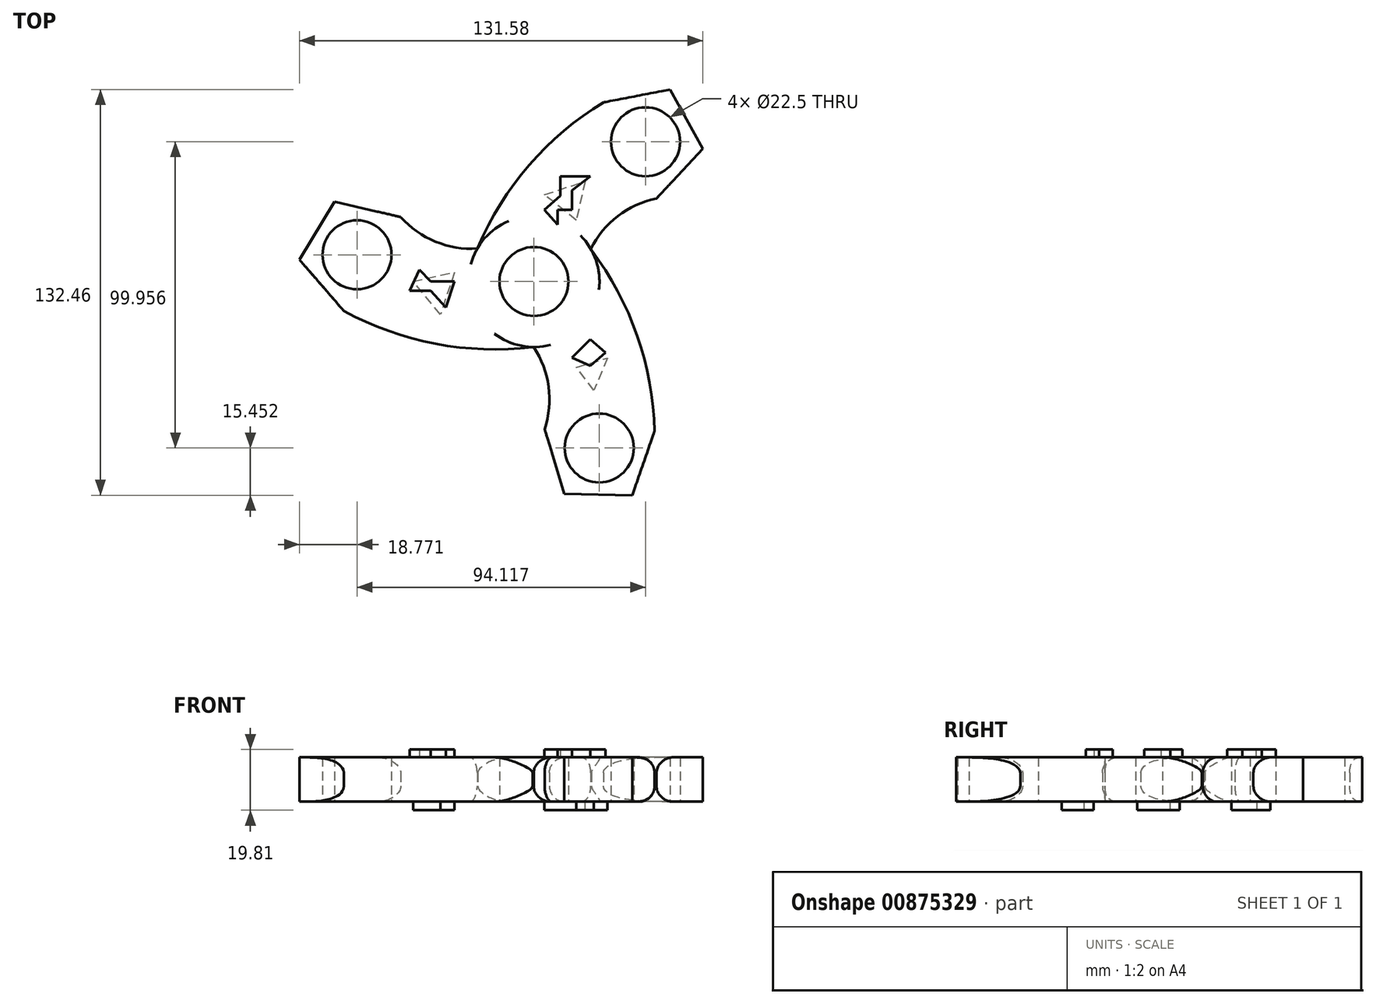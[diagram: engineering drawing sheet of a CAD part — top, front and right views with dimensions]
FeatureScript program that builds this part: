
annotation { "Feature Type Name" : "Feature", "Feature Type Description" : "" }
export const myFeature = defineFeature(function(context is Context, id is Id, definition is map)
    precondition{}
    {
        {
            var Q0;
            Q0=qCreatedBy(makeId("Top.planeOp"),FACE);
            var sketch = newSketch(context, id + "F0", { "sketchPlane" : qUnion([Q0])});
            skCircle(sketch, "E0", {"center": v(0, 0) * mm, "radius": 11.25 * mm});
            skCircle(sketch, "E1", {"center": v(0, 0) * mm, "radius": 21.38 * mm});
            skCircle(sketch, "E2", {"center": v(36.4, 45.62) * mm, "radius": 11.25 * mm});
            skCircle(sketch, "E3.cCircle", {"center": v(36.4, 45.62) * mm, "radius": 15.24 * mm, "construction": true});
            skLineSegment(sketch, "E3.0", {"start": v(22.66, 58.5) * mm, "end": v(44.4, 62.67) * mm});
            skLineSegment(sketch, "E3.1", {"start": v(44.4, 62.67) * mm, "end": v(55.1, 43.28) * mm});
            skLineSegment(sketch, "E3.2", {"start": v(55.1, 43.28) * mm, "end": v(39.96, 27.12) * mm});
            skLineSegment(sketch, "E3.3", {"start": v(39.96, 27.12) * mm, "end": v(19.91, 36.52) * mm});
            skLineSegment(sketch, "E3.4", {"start": v(19.91, 36.52) * mm, "end": v(22.66, 58.5) * mm});
            skPoint(sketch, "E3.0.midPoint", {"position": v(33.53, 60.58) * mm});
            skArc(sketch, "E4", {"start": v(22.66, 58.5) * mm, "mid": v(-1.53, 38) * mm, "end": v(-18.29, 11.09) * mm});
            skArc(sketch, "E5", {"start": v(39.96, 27.12) * mm, "mid": v(27.36, 21.33) * mm, "end": v(18.57, 10.61) * mm});
            skCircle(sketch, "E6.1.0", {"center": v(-57.7, 8.72) * mm, "radius": 15.24 * mm, "construction": true});
            skArc(sketch, "E6.1.1", {"start": v(-61.98, -9.63) * mm, "mid": v(-32.14, -20.32) * mm, "end": v(-0.46, -21.38) * mm});
            skCircle(sketch, "E6.1.2", {"center": v(-57.7, 8.72) * mm, "radius": 11.25 * mm});
            skLineSegment(sketch, "E6.1.3", {"start": v(-41.58, -1.01) * mm, "end": v(-61.98, -9.63) * mm});
            skPoint(sketch, "E6.1.4", {"position": v(-69.23, -1.25) * mm});
            skLineSegment(sketch, "E6.1.6", {"start": v(-43.47, 21.05) * mm, "end": v(-41.58, -1.01) * mm});
            skArc(sketch, "E6.1.7", {"start": v(-43.47, 21.05) * mm, "mid": v(-32.15, 13.03) * mm, "end": v(-18.47, 10.77) * mm});
            skLineSegment(sketch, "E6.1.9", {"start": v(-65.04, 26.08) * mm, "end": v(-43.47, 21.05) * mm});
            skLineSegment(sketch, "E6.1.10", {"start": v(-61.98, -9.63) * mm, "end": v(-76.48, 7.12) * mm});
            skLineSegment(sketch, "E6.1.11", {"start": v(-76.48, 7.12) * mm, "end": v(-65.04, 26.08) * mm});
            skCircle(sketch, "E6.2.0", {"center": v(21.3, -54.34) * mm, "radius": 15.24 * mm, "construction": true});
            skArc(sketch, "E6.2.1", {"start": v(39.33, -48.87) * mm, "mid": v(33.67, -17.68) * mm, "end": v(18.74, 10.3) * mm});
            skCircle(sketch, "E6.2.2", {"center": v(21.3, -54.34) * mm, "radius": 11.25 * mm});
            skLineSegment(sketch, "E6.2.3", {"start": v(21.67, -35.5) * mm, "end": v(39.33, -48.87) * mm});
            skPoint(sketch, "E6.2.4", {"position": v(35.7, -59.33) * mm});
            skLineSegment(sketch, "E6.2.6", {"start": v(3.5, -48.17) * mm, "end": v(21.67, -35.5) * mm});
            skArc(sketch, "E6.2.7", {"start": v(3.5, -48.17) * mm, "mid": v(4.79, -34.36) * mm, "end": v(-0.1, -21.38) * mm});
            skLineSegment(sketch, "E6.2.9", {"start": v(9.94, -69.36) * mm, "end": v(3.5, -48.17) * mm});
            skLineSegment(sketch, "E6.2.10", {"start": v(39.33, -48.87) * mm, "end": v(32.08, -69.8) * mm});
            skLineSegment(sketch, "E6.2.11", {"start": v(32.08, -69.8) * mm, "end": v(9.94, -69.36) * mm});
            skSolve(sketch);
        }
        {
            var Q0;
            Q0=makeQuery(id+"F0.imprint","IMPRINT",FACE,{"disambiguationData":[TD([[makeQuery(id+"F0.imprint","IMPRINT",EDGE,{"derivedFrom":sQuery(id+"F0.wireOp",EDGE,"E0")}),-1.0]])]});
            var Q1;
            Q1=makeQuery(id+"F0.imprint","IMPRINT",FACE,{"disambiguationData":[TD([[makeQuery(id+"F0.imprint","IMPRINT",EDGE,{"derivedFrom":sQuery(id+"F0.wireOp",EDGE,"E3.3")}),1.0]])]});
            var Q2;
            {var subQ1=sQuery(id+"F0.wireOp",EDGE,"E6.2.1");Q2=makeQuery(id+"F0.imprint","IMPRINT",FACE,{"disambiguationData":[TD([[makeQuery(id+"F0.imprint","IMPRINT",EDGE,{"derivedFrom":subQ1}),1.0]])]});}
            var Q3;
            {var subQ1=sQuery(id+"F0.wireOp",EDGE,"E6.1.1");Q3=makeQuery(id+"F0.imprint","IMPRINT",FACE,{"disambiguationData":[TD([[makeQuery(id+"F0.imprint","IMPRINT",EDGE,{"derivedFrom":subQ1}),1.0]])]});}
            var Q4;
            Q4=makeQuery(id+"F0.imprint","IMPRINT",FACE,{"disambiguationData":[TD([[makeQuery(id+"F0.imprint","IMPRINT",EDGE,{"derivedFrom":sQuery(id+"F0.wireOp",EDGE,"E6.1.2")}),-1.0]])]});
            var Q5;
            Q5=makeQuery(id+"F0.imprint","IMPRINT",FACE,{"disambiguationData":[TD([[makeQuery(id+"F0.imprint","IMPRINT",EDGE,{"derivedFrom":sQuery(id+"F0.wireOp",EDGE,"E2")}),-1.0]])]});
            var Q6;
            Q6=makeQuery(id+"F0.imprint","IMPRINT",FACE,{"disambiguationData":[TD([[makeQuery(id+"F0.imprint","IMPRINT",EDGE,{"derivedFrom":sQuery(id+"F0.wireOp",EDGE,"E6.2.2")}),-1.0]])]});
            extrude(context, id + "F1", {"entities" : qUnion([Q0, Q1, Q2, Q3, Q4, Q5, Q6]), "depth" : 14.48 * mm, "offsetDistance" : 25.4 * mm});
        }
        {
            var Q0;
            Q0=qCreatedBy(makeId("Top.planeOp"),FACE);
            var sketch = newSketch(context, id + "F2", { "sketchPlane" : qUnion([Q0])});
            skLineSegment(sketch, "E7", {"start": v(-30.5, -10.8) * mm, "end": v(-39.42, 0) * mm});
            skLineSegment(sketch, "E8", {"start": v(-39.42, 0) * mm, "end": v(-25.9, 3.02) * mm});
            skLineSegment(sketch, "E9", {"start": v(-25.9, 3.02) * mm, "end": v(-30.5, -10.8) * mm});
            skLineSegment(sketch, "E10", {"start": v(13.82, 20) * mm, "end": v(3.46, 28.35) * mm});
            skLineSegment(sketch, "E11", {"start": v(3.46, 28.35) * mm, "end": v(16.7, 32.67) * mm});
            skLineSegment(sketch, "E12", {"start": v(16.7, 32.67) * mm, "end": v(13.82, 20) * mm});
            skLineSegment(sketch, "E13", {"start": v(19.55, -35.48) * mm, "end": v(13.82, -28.06) * mm});
            skLineSegment(sketch, "E14", {"start": v(13.82, -28.06) * mm, "end": v(23.94, -25.02) * mm});
            skLineSegment(sketch, "E15", {"start": v(23.94, -25.02) * mm, "end": v(19.55, -35.48) * mm});
            skSolve(sketch);
        }
        {
            var Q0;
            Q0 = qSketchRegion(id + "F2", true);
            extrude(context, id + "F3", {"entities" : qUnion([Q0]), "operationType" : NewBodyOperationType.ADD, "oppositeDirection" : true, "depth" : 2.8 * mm, "offsetDistance" : 25.4 * mm});
        }
        {
            var Q0;
            Q0=makeQuery(id+"F1.opExtrude","CAP_FACE",FACE,{"disambiguationData":[OSD([sQuery(id+"F0.wireOp",EDGE,"E2"),sQuery(id+"F0.wireOp",EDGE,"E3.0"),sQuery(id+"F0.wireOp",EDGE,"E3.1"),sQuery(id+"F0.wireOp",EDGE,"E3.2"),sQuery(id+"F0.wireOp",EDGE,"E4"),sQuery(id+"F0.wireOp",EDGE,"E5"),sQuery(id+"F0.wireOp",EDGE,"E6.1.1"),sQuery(id+"F0.wireOp",EDGE,"E6.1.2"),sQuery(id+"F0.wireOp",EDGE,"E6.1.7"),sQuery(id+"F0.wireOp",EDGE,"E6.1.9"),sQuery(id+"F0.wireOp",EDGE,"E6.1.10"),sQuery(id+"F0.wireOp",EDGE,"E6.1.11"),sQuery(id+"F0.wireOp",EDGE,"E6.2.1"),sQuery(id+"F0.wireOp",EDGE,"E6.2.2"),sQuery(id+"F0.wireOp",EDGE,"E1"),sQuery(id+"F0.wireOp",EDGE,"E6.2.7"),sQuery(id+"F0.wireOp",EDGE,"E0"),sQuery(id+"F0.wireOp",EDGE,"E6.2.9"),sQuery(id+"F0.wireOp",EDGE,"E6.2.10"),sQuery(id+"F0.wireOp",EDGE,"E6.2.11")])],"isStart":false});
            var sketch = newSketch(context, id + "F4", { "sketchPlane" : qUnion([Q0])});
            skSolve(sketch);
        }
        {
            var Q0;
            Q0=makeQuery(id+"F4.imprint","IMPRINT",FACE,{"disambiguationData":[TD([[makeQuery(id+"F4.imprint","IMPRINT",EDGE,{"derivedFrom":makeQuery(id+"F1.opExtrude","CAP_EDGE",EDGE,{"disambiguationData":[OSD([sQuery(id+"F0.wireOp",EDGE,"E2")])],"isStart":false})}),-1.0]])]});
            var sketch = newSketch(context, id + "F5", { "sketchPlane" : qUnion([Q0])});
            skLineSegment(sketch, "E16", {"start": v(-37.41, 3.89) * mm, "end": v(-40.58, -3.02) * mm});
            skLineSegment(sketch, "E17", {"start": v(-40.58, -3.02) * mm, "end": v(-33.67, -3.02) * mm});
            skLineSegment(sketch, "E18", {"start": v(-33.67, -3.02) * mm, "end": v(-28.78, -8.5) * mm});
            skLineSegment(sketch, "E19", {"start": v(-28.78, -8.5) * mm, "end": v(-25.9, 0) * mm});
            skLineSegment(sketch, "E20", {"start": v(-25.9, 0) * mm, "end": v(-33.67, 0) * mm});
            skLineSegment(sketch, "E21", {"start": v(-33.67, 0) * mm, "end": v(-37.41, 3.89) * mm});
            skLineSegment(sketch, "E22", {"start": v(10.94, 34.4) * mm, "end": v(18.42, 34.4) * mm});
            skLineSegment(sketch, "E23", {"start": v(18.42, 34.4) * mm, "end": v(12.38, 29.79) * mm});
            skLineSegment(sketch, "E24", {"start": v(12.38, 29.79) * mm, "end": v(12.38, 23.46) * mm});
            skLineSegment(sketch, "E25", {"start": v(12.38, 23.46) * mm, "end": v(7.78, 23.46) * mm});
            skLineSegment(sketch, "E26", {"start": v(7.78, 23.46) * mm, "end": v(7.78, 18.56) * mm});
            skLineSegment(sketch, "E27", {"start": v(7.78, 18.56) * mm, "end": v(3.46, 23.46) * mm});
            skLineSegment(sketch, "E28", {"start": v(3.46, 23.46) * mm, "end": v(8.59, 27.98) * mm});
            skLineSegment(sketch, "E29", {"start": v(8.59, 27.98) * mm, "end": v(8.59, 34.4) * mm});
            skLineSegment(sketch, "E30", {"start": v(8.59, 34.4) * mm, "end": v(10.94, 34.4) * mm});
            skLineSegment(sketch, "E31", {"start": v(23.32, -23.17) * mm, "end": v(18.42, -27.49) * mm});
            skLineSegment(sketch, "E32", {"start": v(18.42, -27.49) * mm, "end": v(12.38, -24.9) * mm});
            skLineSegment(sketch, "E33", {"start": v(12.38, -24.9) * mm, "end": v(18.42, -18.85) * mm});
            skLineSegment(sketch, "E34", {"start": v(18.42, -18.85) * mm, "end": v(23.32, -23.17) * mm});
            skSolve(sketch);
        }
        {
            var Q0;
            Q0 = qSketchRegion(id + "F5", true);
            extrude(context, id + "F6", {"entities" : qUnion([Q0]), "operationType" : NewBodyOperationType.ADD, "depth" : 2.54 * mm, "offsetDistance" : 25.4 * mm});
        }
        {
            var Q0;
            Q0=makeQuery(id+"F1.opExtrude","CAP_EDGE",EDGE,{"disambiguationData":[OSD([sQuery(id+"F0.wireOp",EDGE,"E6.1.1")])],"isStart":false});
            var Q1;
            Q1=makeQuery(id+"F1.opExtrude","CAP_EDGE",EDGE,{"disambiguationData":[OSD([sQuery(id+"F0.wireOp",EDGE,"E6.2.1")])],"isStart":false});
            var Q2;
            Q2=makeQuery(id+"F1.opExtrude","CAP_EDGE",EDGE,{"disambiguationData":[OSD([sQuery(id+"F0.wireOp",EDGE,"E5")])],"isStart":false});
            var Q3;
            Q3=makeQuery(id+"F1.opExtrude","CAP_EDGE",EDGE,{"disambiguationData":[OSD([sQuery(id+"F0.wireOp",EDGE,"E5")])],"isStart":true});
            var Q4;
            Q4=makeQuery(id+"F1.opExtrude","CAP_EDGE",EDGE,{"disambiguationData":[OSD([sQuery(id+"F0.wireOp",EDGE,"E6.2.1")])],"isStart":true});
            var Q5;
            Q5=makeQuery(id+"F1.opExtrude","CAP_EDGE",EDGE,{"disambiguationData":[OSD([sQuery(id+"F0.wireOp",EDGE,"E6.1.1")])],"isStart":true});
            var Q6;
            Q6=makeQuery(id+"F1.opExtrude","CAP_EDGE",EDGE,{"disambiguationData":[OSD([sQuery(id+"F0.wireOp",EDGE,"E6.1.7")])],"isStart":false});
            var Q7;
            Q7=makeQuery(id+"F1.opExtrude","CAP_EDGE",EDGE,{"disambiguationData":[OSD([sQuery(id+"F0.wireOp",EDGE,"E4")])],"isStart":false});
            var Q8;
            Q8=makeQuery(id+"F1.opExtrude","CAP_EDGE",EDGE,{"disambiguationData":[OSD([sQuery(id+"F0.wireOp",EDGE,"E6.1.7")])],"isStart":true});
            var Q9;
            Q9=makeQuery(id+"F1.opExtrude","CAP_EDGE",EDGE,{"disambiguationData":[OSD([sQuery(id+"F0.wireOp",EDGE,"E4")])],"isStart":true});
            fillet(context, id + "F7", {"entities" : qUnion([Q0, Q1, Q2, Q3, Q4, Q5, Q6, Q7, Q8, Q9]), "radius" : 5.08 * mm, "tangentPropagation" : true, "allowEdgeOverflow" : false});
        }
        {
            var Q0;
            Q0=makeQuery(id+"F1.opExtrude","CAP_EDGE",EDGE,{"disambiguationData":[OSD([sQuery(id+"F0.wireOp",EDGE,"E6.2.7")])],"isStart":false});
            var Q1;
            Q1=makeQuery(id+"F1.opExtrude","CAP_EDGE",EDGE,{"disambiguationData":[OSD([sQuery(id+"F0.wireOp",EDGE,"E6.2.7")])],"isStart":true});
            fillet(context, id + "F8", {"entities" : qUnion([Q0, Q1]), "radius" : 5.08 * mm, "tangentPropagation" : true, "allowEdgeOverflow" : false});
        }
    });
